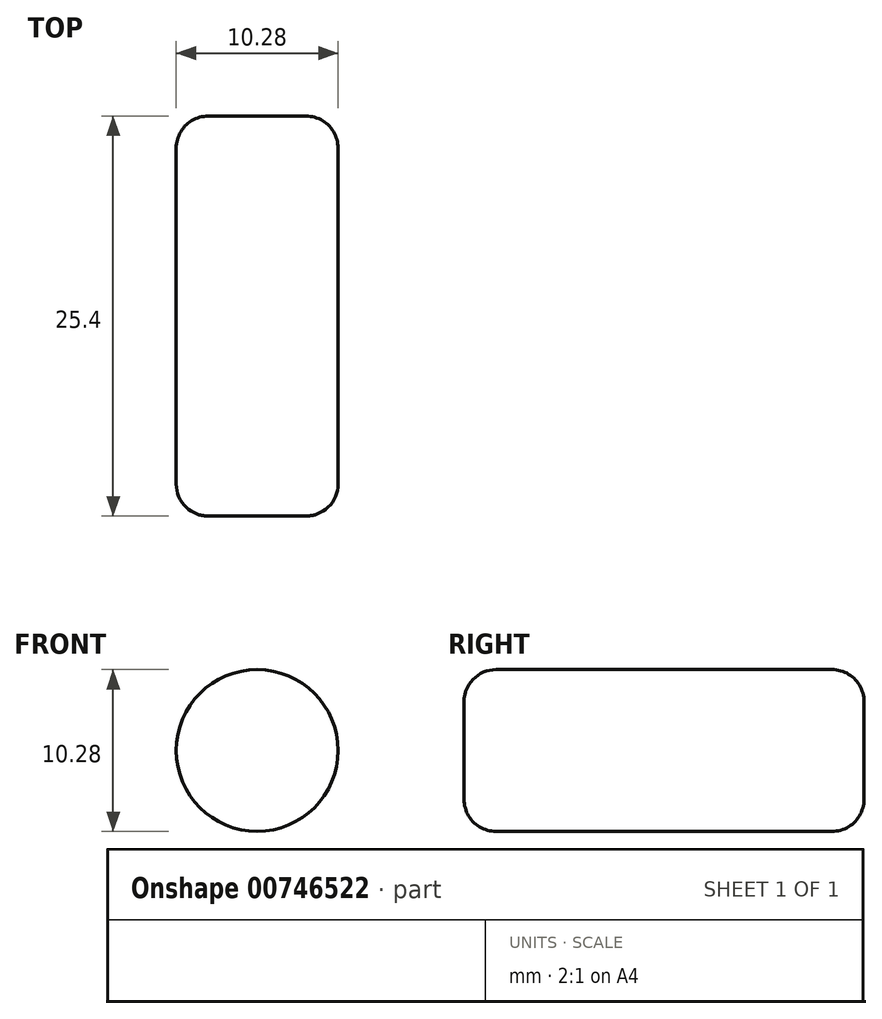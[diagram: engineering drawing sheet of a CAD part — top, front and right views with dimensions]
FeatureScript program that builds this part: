
annotation { "Feature Type Name" : "Feature", "Feature Type Description" : "" }
export const myFeature = defineFeature(function(context is Context, id is Id, definition is map)
    precondition{}
    {
        {
            var Q0;
            Q0=qCreatedBy(makeId("Front.planeOp"),FACE);
            var sketch = newSketch(context, id + "F0", { "sketchPlane" : qUnion([Q0])});
            skCircle(sketch, "E0", {"center": v(-21.67, 17.6) * mm, "radius": 5.14 * mm});
            skSolve(sketch);
        }
        {
            var Q0;
            Q0=makeQuery(id+"F0.imprint","IMPRINT",FACE,{"disambiguationData":[TD([[makeQuery(id+"F0.imprint","IMPRINT",EDGE,{"derivedFrom":sQuery(id+"F0.wireOp",EDGE,"E0")}),1.0]])]});
            extrude(context, id + "F1", {"entities" : qUnion([Q0]), "depth" : 25.4 * mm, "offsetDistance" : 25.4 * mm});
        }
        {
            var Q0;
            Q0=makeQuery(id+"F1.opExtrude","CAP_EDGE",EDGE,{"disambiguationData":[OSD([sQuery(id+"F0.wireOp",EDGE,"E0")])],"isStart":true});
            var Q1;
            Q1=makeQuery(id+"F1.opExtrude","CAP_EDGE",EDGE,{"disambiguationData":[OSD([sQuery(id+"F0.wireOp",EDGE,"E0")])],"isStart":false});
            fillet(context, id + "F2", {"entities" : qUnion([Q0, Q1]), "radius" : 2.03 * mm, "tangentPropagation" : true, "allowEdgeOverflow" : false});
        }
    });
